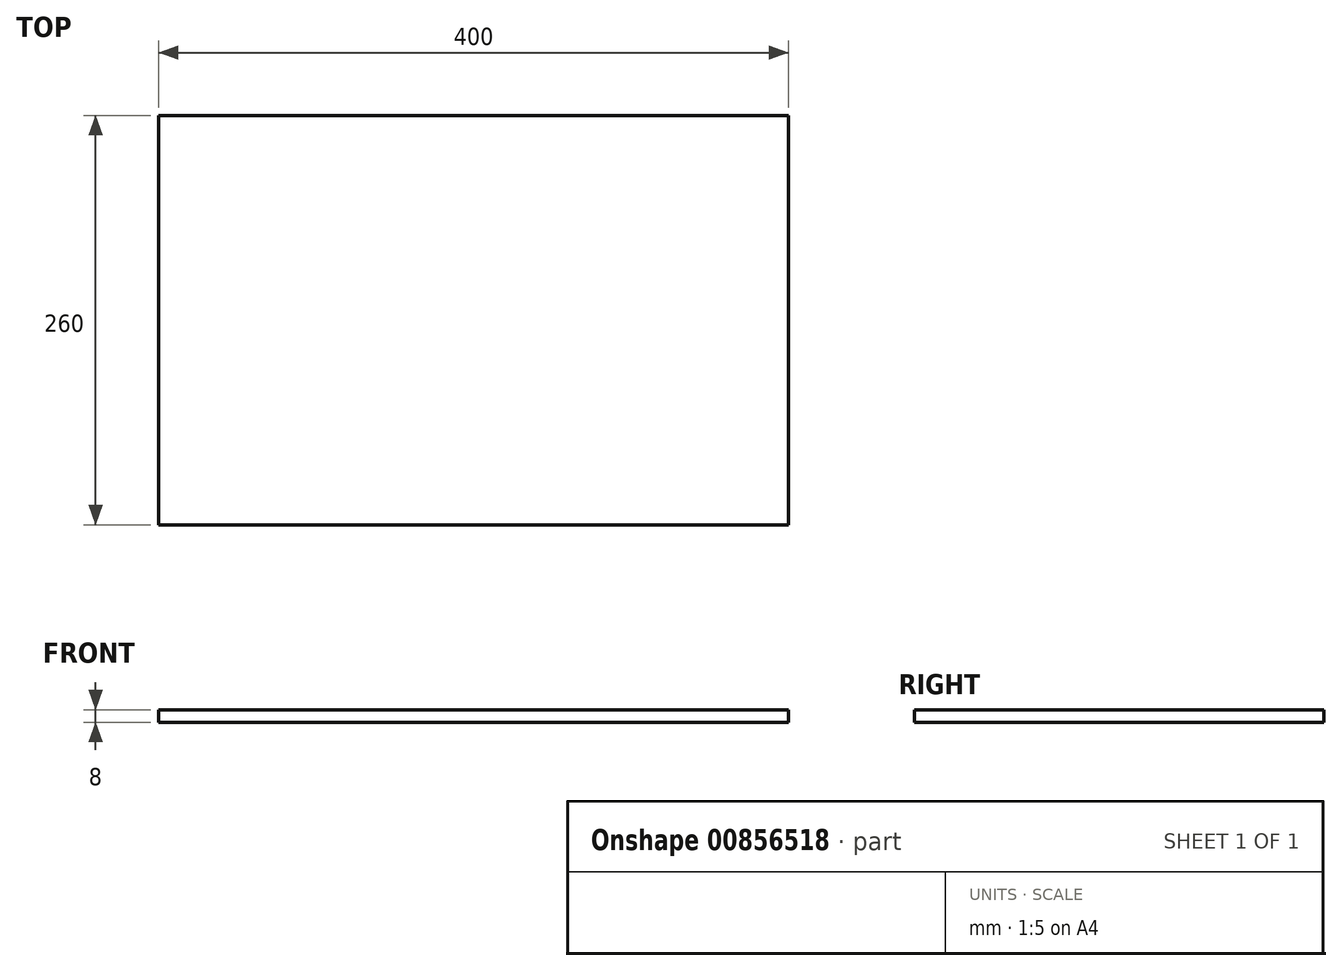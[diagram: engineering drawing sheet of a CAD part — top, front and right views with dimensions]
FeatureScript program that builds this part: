
annotation { "Feature Type Name" : "Feature", "Feature Type Description" : "" }
export const myFeature = defineFeature(function(context is Context, id is Id, definition is map)
    precondition{}
    {
        {
            var Q0;
            Q0=qCreatedBy(makeId("Top.planeOp"),FACE);
            var sketch = newSketch(context, id + "F0", { "sketchPlane" : qUnion([Q0])});
            skLineSegment(sketch, "E0.bottom", {"start": v(200, 130) * mm, "end": v(-200, 130) * mm});
            skLineSegment(sketch, "E0.top", {"start": v(200, -130) * mm, "end": v(-200, -130) * mm});
            skLineSegment(sketch, "E0.left", {"start": v(200, 130) * mm, "end": v(200, -130) * mm});
            skLineSegment(sketch, "E0.right", {"start": v(-200, 130) * mm, "end": v(-200, -130) * mm});
            skPoint(sketch, "E0.middle", {"position": v(0, 0) * mm});
            skSolve(sketch);
        }
        {
            var Q0;
            Q0=makeQuery(id+"F0.imprint","IMPRINT",FACE,{"disambiguationData":[TD([[makeQuery(id+"F0.imprint","IMPRINT",EDGE,{"derivedFrom":sQuery(id+"F0.wireOp",EDGE,"E0.bottom")}),1.0]])]});
            extrude(context, id + "F1", {"entities" : qUnion([Q0]), "depth" : 8 * mm, "offsetDistance" : 25 * mm});
        }
    });
